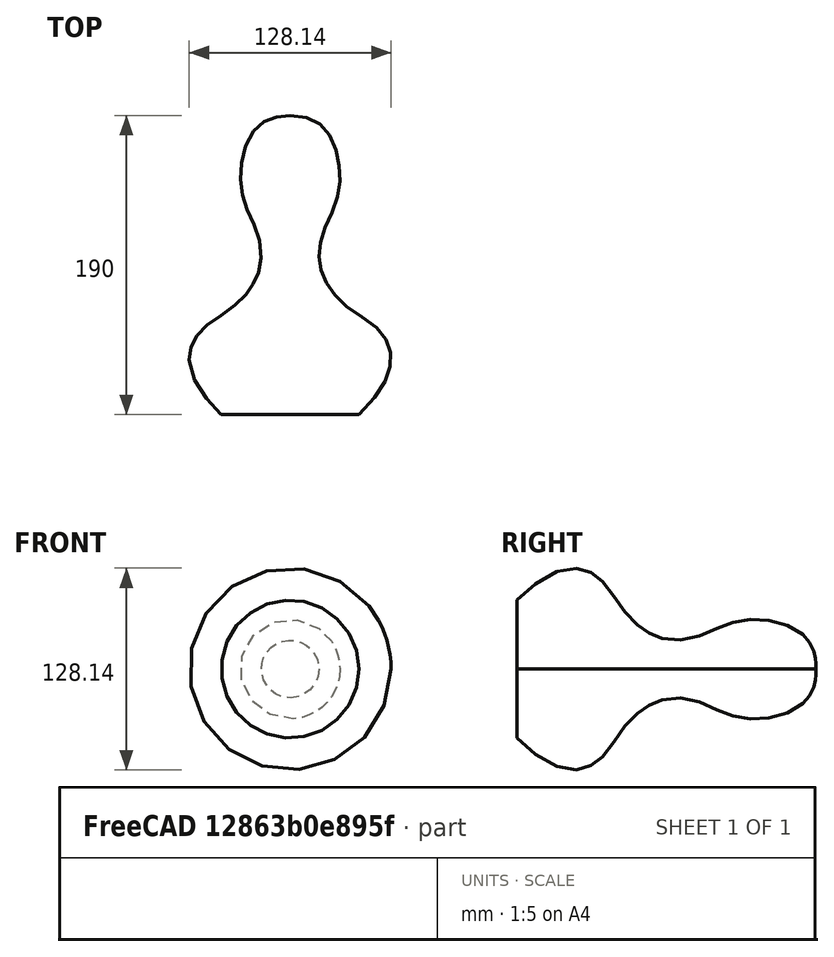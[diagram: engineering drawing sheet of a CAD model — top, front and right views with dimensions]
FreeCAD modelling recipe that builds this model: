
FCSTD DOCUMENT  (FreeCAD 0.20R29410 (Git))
Label: MangoJelly_Solutions_Tutorial_Ep11_1
License: All rights reserved
LicenseURL: http://en.wikipedia.org/wiki/All_rights_reserved
objects: Sketcher::SketchObject×6, Part::Loft×1
note: 7 computed .brp shape members not serialized (recipe doc carries the construction recipe); baked Part::Feature solids carry a one-line shape summary decoded from their .brp

FEATURE [Sketcher::SketchObject] Sketch
  FullyConstrained = false
  Placement = pos=(0,0,0) rot=(1,0,0;1.5708rad)
  sketch-geometry (1):
    g0: Circle CenterX=0 CenterY=0 CenterZ=0 NormalX=0 NormalY=0 NormalZ=1 AngleXU=0 Radius=43.7662
  constraints (1):
    c: Coincident(g0,g-1)
FEATURE [Sketcher::SketchObject] Sketch001
  FullyConstrained = false
  Placement = pos=(0,50,0) rot=(1,0,0;1.5708rad)
  sketch-geometry (1):
    g0: Circle CenterX=0 CenterY=0 CenterZ=0 NormalX=0 NormalY=0 NormalZ=1 AngleXU=0 Radius=59.4239
  constraints (1):
    c: Coincident(g0,g-1)
FEATURE [Sketcher::SketchObject] Sketch002
  FullyConstrained = false
  Placement = pos=(0,100,0) rot=(1,0,0;1.5708rad)
  sketch-geometry (1):
    g0: Circle CenterX=0 CenterY=0 CenterZ=0 NormalX=0 NormalY=0 NormalZ=1 AngleXU=0 Radius=18.333
  constraints (1):
    c: Coincident(g0,g-1)
FEATURE [Sketcher::SketchObject] Sketch003
  FullyConstrained = false
  Placement = pos=(0,150,0) rot=(1,0,0;1.5708rad)
  sketch-geometry (1):
    g0: Circle CenterX=0 CenterY=0 CenterZ=0 NormalX=0 NormalY=0 NormalZ=1 AngleXU=0 Radius=31.5917
  constraints (1):
    c: Coincident(g0,g-1)
FEATURE [Sketcher::SketchObject] Sketch004
  FullyConstrained = false
  Placement = pos=(0,180,0) rot=(1,0,0;1.5708rad)
  sketch-geometry (1):
    g0: Circle CenterX=0 CenterY=0 CenterZ=0 NormalX=0 NormalY=0 NormalZ=1 AngleXU=0 Radius=23.2814
  constraints (1):
    c: Coincident(g0,g-1)
FEATURE [Sketcher::SketchObject] Sketch005
  FullyConstrained = true
  Placement = pos=(0,190,0) rot=(1,0,0;1.5708rad)
  sketch-geometry (1):
    g0: GeomPoint X=0 Y=0 Z=0
  constraints (1):
    c: Coincident(g0,g-1)
FEATURE [Part::Loft] Loft
  Closed = false
  MaxDegree = 2
  Ruled = false
  Sections = -> [Sketch,Sketch001,Sketch002,Sketch003,Sketch004,Sketch005]
  Solid = true
